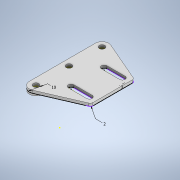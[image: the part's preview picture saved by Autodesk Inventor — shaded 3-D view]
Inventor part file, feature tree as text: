
AUTODESK INVENTOR PART (.ipt)
format: ipt  version: 2022.2 (Build 262287000, 287)  size: 168,960 bytes
history: native  units: mm
features: sketch x2, extrude x2, other x1
ambient origin geometry x8: Origin, YZ Plane, XZ Plane, XY Plane, X Axis, Y Axis, Z Axis, Center Point
bodies: Solid1 (feature_tree)
feature tree (5):
  other  "Straigthener.ipt"
  sketch  "Sketch2"  dims[d2=2.0mm d3=0.0mm d4=1.5mm d5=0.0mm d6=2.0mm d7=3.0mm]
  extrude  "Extrusion1"  Depth=10.0mm
  extrude  "Extrusion2"  Depth=1.5mm TaperAngle=0.0deg
  sketch  "Sketch1"  dims[d0=10.0mm d1=10.0mm]
